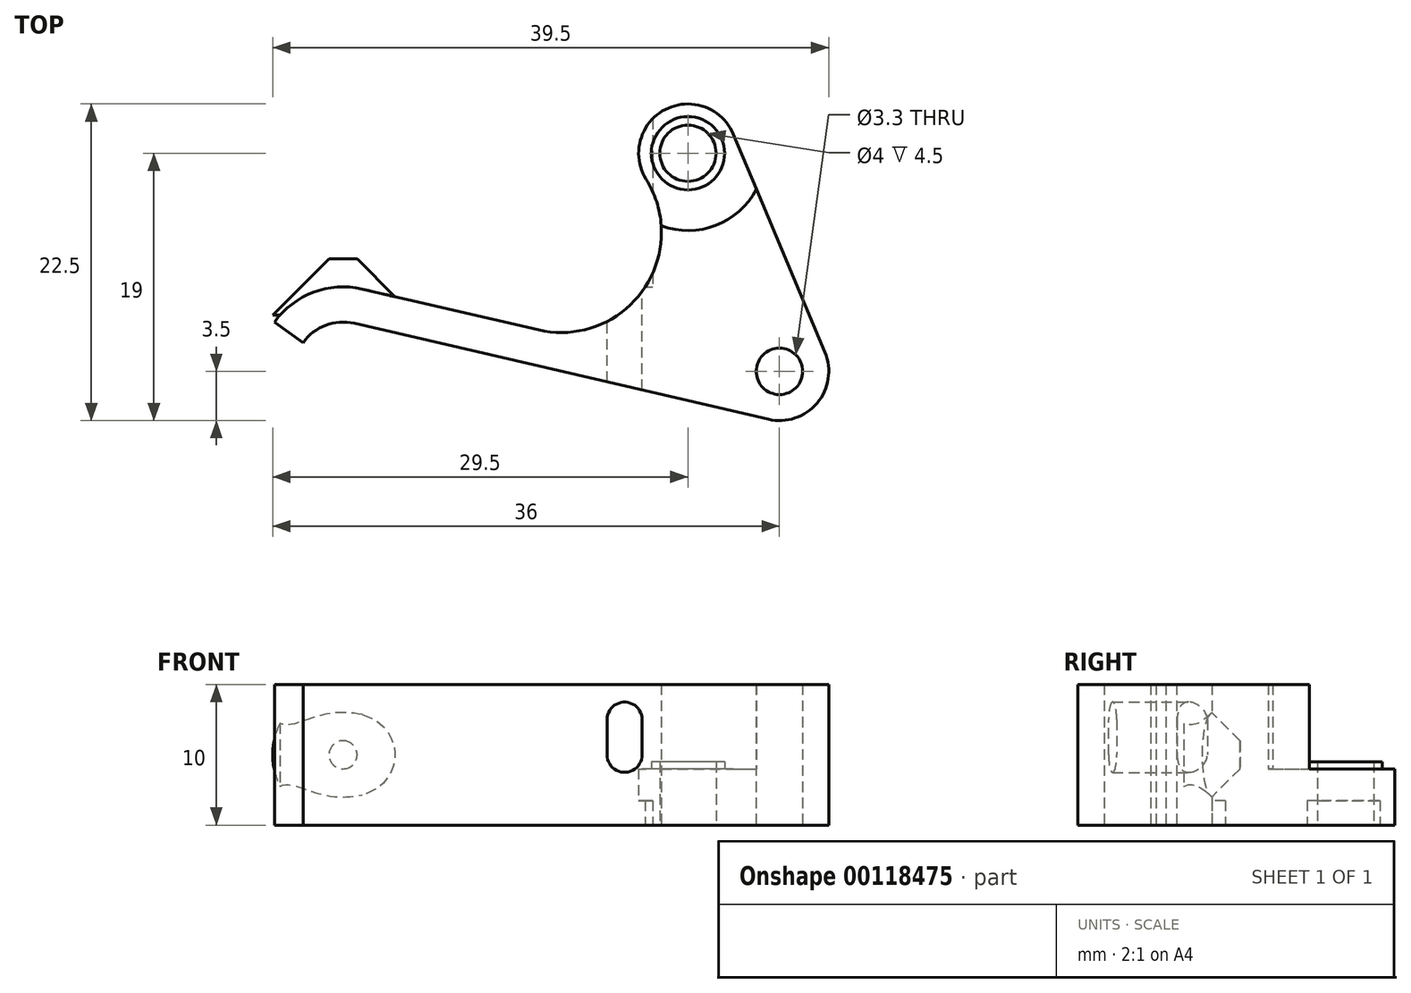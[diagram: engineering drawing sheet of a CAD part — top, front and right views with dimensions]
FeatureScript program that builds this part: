
annotation { "Feature Type Name" : "Feature", "Feature Type Description" : "" }
export const myFeature = defineFeature(function(context is Context, id is Id, definition is map)
    precondition{}
    {
        {
            var Q0;
            Q0=qCreatedBy(makeId("Top.planeOp"),FACE);
            var sketch = newSketch(context, id + "F0", { "sketchPlane" : qUnion([Q0])});
            skCircle(sketch, "E0", {"center": v(0, 0) * mm, "radius": 4.5 * mm, "construction": true});
            skCircle(sketch, "E1", {"center": v(9, 0) * mm, "radius": 4.5 * mm, "construction": true});
            skLineSegment(sketch, "E2.bottom", {"start": v(15.5, 15.5) * mm, "end": v(-15.5, 15.5) * mm, "construction": true});
            skLineSegment(sketch, "E2.top", {"start": v(15.5, -15.5) * mm, "end": v(-15.5, -15.5) * mm, "construction": true});
            skLineSegment(sketch, "E2.left", {"start": v(15.5, 15.5) * mm, "end": v(15.5, -15.5) * mm, "construction": true});
            skLineSegment(sketch, "E2.right", {"start": v(-15.5, 15.5) * mm, "end": v(-15.5, -15.5) * mm, "construction": true});
            skLineSegment(sketch, "E3.bottom", {"start": v(21, 21) * mm, "end": v(-21, 21) * mm, "construction": true});
            skLineSegment(sketch, "E3.top", {"start": v(21, -21) * mm, "end": v(-21, -21) * mm, "construction": true});
            skLineSegment(sketch, "E3.left", {"start": v(21, 21) * mm, "end": v(21, -21) * mm, "construction": true});
            skLineSegment(sketch, "E3.right", {"start": v(-21, 21) * mm, "end": v(-21, -21) * mm, "construction": true});
            skPoint(sketch, "E4", {"position": v(15.5, 0) * mm});
            skCircle(sketch, "E5", {"center": v(15.5, -15.5) * mm, "radius": 1.65 * mm});
            skCircle(sketch, "E6", {"center": v(15.5, -15.5) * mm, "radius": 3.5 * mm});
            skLineSegment(sketch, "E7", {"start": v(-14.7, -12.1) * mm, "end": v(14.7, -18.9) * mm});
            skLineSegment(sketch, "E8", {"start": v(12.23, 1.35) * mm, "end": v(18.73, -14.15) * mm});
            skLineSegment(sketch, "E9", {"start": v(-15.5, -15.5) * mm, "end": v(-14.7, -12.1) * mm, "construction": true});
            skLineSegment(sketch, "E10", {"start": v(-14.7, -12.1) * mm, "end": v(-14.15, -9.65) * mm, "construction": true});
            skLineSegment(sketch, "E11", {"start": v(-14.15, -9.65) * mm, "end": v(-1.6, -12.56) * mm});
            skArc(sketch, "E12", {"start": v(-1.6, -12.56) * mm, "mid": v(5.8, -9.76) * mm, "end": v(6.03, -1.86) * mm});
            skArc(sketch, "E13", {"start": v(7.1, -5.16) * mm, "mid": v(10.97, -5.13) * mm, "end": v(13.87, -2.56) * mm});
            skArc(sketch, "E14", {"start": v(13.87, -2.56) * mm, "mid": v(7.03, 5.13) * mm, "end": v(7.1, -5.16) * mm, "construction": true});
            skArc(sketch, "E15", {"start": v(6.03, -1.86) * mm, "mid": v(10.61, -3.1) * mm, "end": v(12.23, 1.35) * mm, "construction": true});
            skArc(sketch, "E16", {"start": v(12.23, 1.35) * mm, "mid": v(7.39, 3.1) * mm, "end": v(6.03, -1.86) * mm});
            skLineSegment(sketch, "E17", {"start": v(-15.5, -12) * mm, "end": v(-20.37, -12) * mm, "construction": true});
            skLineSegment(sketch, "E18", {"start": v(-20.37, -12) * mm, "end": v(-18.34, -13.46) * mm});
            skLineSegment(sketch, "E19", {"start": v(-18.34, -13.46) * mm, "end": v(-15.5, -15.5) * mm, "construction": true});
            skArc(sketch, "E20", {"start": v(-20.37, -12) * mm, "mid": v(-16.18, -21.46) * mm, "end": v(-9.96, -13.2) * mm, "construction": true});
            skArc(sketch, "E21", {"start": v(-9.96, -13.2) * mm, "mid": v(-11.63, -10.92) * mm, "end": v(-14.15, -9.65) * mm, "construction": true});
            skArc(sketch, "E22", {"start": v(-14.15, -9.65) * mm, "mid": v(-17.61, -9.88) * mm, "end": v(-20.37, -12) * mm});
            skArc(sketch, "E23", {"start": v(-18.34, -13.46) * mm, "mid": v(-14.27, -18.78) * mm, "end": v(-14.7, -12.1) * mm, "construction": true});
            skArc(sketch, "E24", {"start": v(-14.7, -12.1) * mm, "mid": v(-16.73, -12.22) * mm, "end": v(-18.34, -13.46) * mm});
            skCircle(sketch, "E25", {"center": v(9, 0) * mm, "radius": 2.6 * mm});
            skCircle(sketch, "E26", {"center": v(9, 0) * mm, "radius": 2 * mm});
            skLineSegment(sketch, "E27", {"start": v(4.5, 0) * mm, "end": v(4.5, -21) * mm, "construction": true});
            skSolve(sketch);
        }
        {
            var Q0;
            {var subQ5=sQuery(id+"F0.wireOp",EDGE,"E7");Q0=makeQuery(id+"F0.imprint","IMPRINT",FACE,{"disambiguationData":[TD([[makeQuery(id+"F0.imprint","IMPRINT",EDGE,{"derivedFrom":subQ5}),1.0]])]});}
            var Q1;
            Q1=makeQuery(id+"F0.imprint","IMPRINT",FACE,{"disambiguationData":[TD([[makeQuery(id+"F0.imprint","IMPRINT",EDGE,{"derivedFrom":sQuery(id+"F0.wireOp",EDGE,"E5")}),-1.0]])]});
            extrude(context, id + "F1", {"entities" : qUnion([Q0, Q1]), "depth" : 10 * mm});
        }
        {
            var Q0;
            {var subQ1=sQuery(id+"F0.wireOp",EDGE,"E13");Q0=makeQuery(id+"F0.imprint","IMPRINT",FACE,{"disambiguationData":[TD([[makeQuery(id+"F0.imprint","IMPRINT",EDGE,{"derivedFrom":subQ1}),1.0]])]});}
            extrude(context, id + "F2", {"entities" : qUnion([Q0]), "operationType" : NewBodyOperationType.ADD, "depth" : 4 * mm});
        }
        {
            var Q0;
            Q0=makeQuery(id+"F0.imprint","IMPRINT",FACE,{"disambiguationData":[TD([[makeQuery(id+"F0.imprint","IMPRINT",EDGE,{"derivedFrom":sQuery(id+"F0.wireOp",EDGE,"E25")}),1.0]])]});
            extrude(context, id + "F3", {"entities" : qUnion([Q0]), "operationType" : NewBodyOperationType.ADD, "depth" : 4.5 * mm});
        }
        {
            var Q0;
            Q0=qCreatedBy(makeId("Front.planeOp"),FACE);
            cPlane(context, id + "F4", {"entities" : qUnion([Q0]), "cplaneType" : CPlaneType.OFFSET, "offset" : 9.5 * mm, "width" : 150 * mm, "height" : 150 * mm});
        }
        {
            var Q0;
            Q0=qCreatedBy(id+"F4.planeOp",FACE);
            var sketch = newSketch(context, id + "F5", { "sketchPlane" : qUnion([Q0])});
            skCircle(sketch, "E28", {"center": v(-15.5, 5) * mm, "radius": 3 * mm});
            skPoint(sketch, "E29", {"position": v(-15.5, 0) * mm});
            skPoint(sketch, "E30", {"position": v(4.5, 0) * mm});
            skCircle(sketch, "E31", {"center": v(4.5, 5) * mm, "radius": 1.25 * mm});
            skCircle(sketch, "E32", {"center": v(4.5, 7.5) * mm, "radius": 1.25 * mm});
            skLineSegment(sketch, "E33", {"start": v(3.25, 7.5) * mm, "end": v(3.25, 5) * mm});
            skLineSegment(sketch, "E34", {"start": v(5.75, 5) * mm, "end": v(5.75, 7.5) * mm});
            skLineSegment(sketch, "E35.bottom", {"start": v(4.5, 0) * mm, "end": v(6.5, 0) * mm});
            skLineSegment(sketch, "E35.top", {"start": v(4.5, 1.75) * mm, "end": v(6.5, 1.75) * mm});
            skLineSegment(sketch, "E35.left", {"start": v(4.5, 0) * mm, "end": v(4.5, 1.75) * mm});
            skLineSegment(sketch, "E35.right", {"start": v(6.5, 0) * mm, "end": v(6.5, 1.75) * mm});
            skSolve(sketch);
        }
        {
            var Q0;
            Q0=makeQuery(id+"F5.imprint","IMPRINT",FACE,{"disambiguationData":[TD([[makeQuery(id+"F5.imprint","IMPRINT",EDGE,{"derivedFrom":sQuery(id+"F5.wireOp",EDGE,"E28")}),1.0]])]});
            extrude(context, id + "F6", {"entities" : qUnion([Q0]), "operationType" : NewBodyOperationType.ADD, "oppositeDirection" : true, "depth" : 2 * mm, "hasDraft" : true, "draftAngle" : 45 * degree, "draftPullDirection" : true, "hasSecondDirection" : true, "secondDirectionOppositeDirection" : false, "secondDirectionDepth" : 2 * mm, "hasSecondDirectionDraft" : true, "secondDirectionDraftAngle" : 45 * degree});
        }
        {
            var Q0;
            Q0=makeQuery(id+"F5.imprint","IMPRINT",FACE,{"disambiguationData":[TD([[makeQuery(id+"F5.imprint","IMPRINT",EDGE,{"derivedFrom":sQuery(id+"F5.wireOp",EDGE,"E31")}),1.0]])]});
            var Q1;
            {var subQ0=sQuery(id+"F5.wireOp",EDGE,"E32");var subQ1=makeQuery(id+"F5.imprint","INTERSECT",VERTEX,{"derivedFrom":[subQ0,sQuery(id+"F5.wireOp",EDGE,"E33")]});Q1=makeQuery(id+"F5.imprint","IMPRINT",FACE,{"disambiguationData":[TD([[makeQuery(id+"F5.imprint","IMPRINT",EDGE,{"disambiguationData":[TD([[subQ1,1.0]])],"derivedFrom":subQ0}),1.0]])]});}
            var Q2;
            {var subQ0=sQuery(id+"F5.wireOp",EDGE,"E33");Q2=makeQuery(id+"F5.imprint","IMPRINT",FACE,{"disambiguationData":[TD([[makeQuery(id+"F5.imprint","IMPRINT",EDGE,{"derivedFrom":subQ0}),1.0]])]});}
            var Q3;
            {var subQ0=sQuery(id+"F5.wireOp",EDGE,"E34");Q3=makeQuery(id+"F5.imprint","IMPRINT",FACE,{"disambiguationData":[TD([[makeQuery(id+"F5.imprint","IMPRINT",EDGE,{"derivedFrom":subQ0}),1.0]])]});}
            extrude(context, id + "F7", {"entities" : qUnion([Q0, Q1, Q2, Q3]), "operationType" : NewBodyOperationType.REMOVE, "depth" : 25 * mm});
        }
        {
            var Q0;
            Q0=makeQuery(id+"F5.imprint","IMPRINT",FACE,{"disambiguationData":[TD([[makeQuery(id+"F5.imprint","IMPRINT",EDGE,{"derivedFrom":sQuery(id+"F5.wireOp",EDGE,"E35.bottom")}),1.0]])]});
            extrude(context, id + "F8", {"entities" : qUnion([Q0]), "operationType" : NewBodyOperationType.REMOVE, "oppositeDirection" : true, "depth" : 25 * mm});
        }
    });
